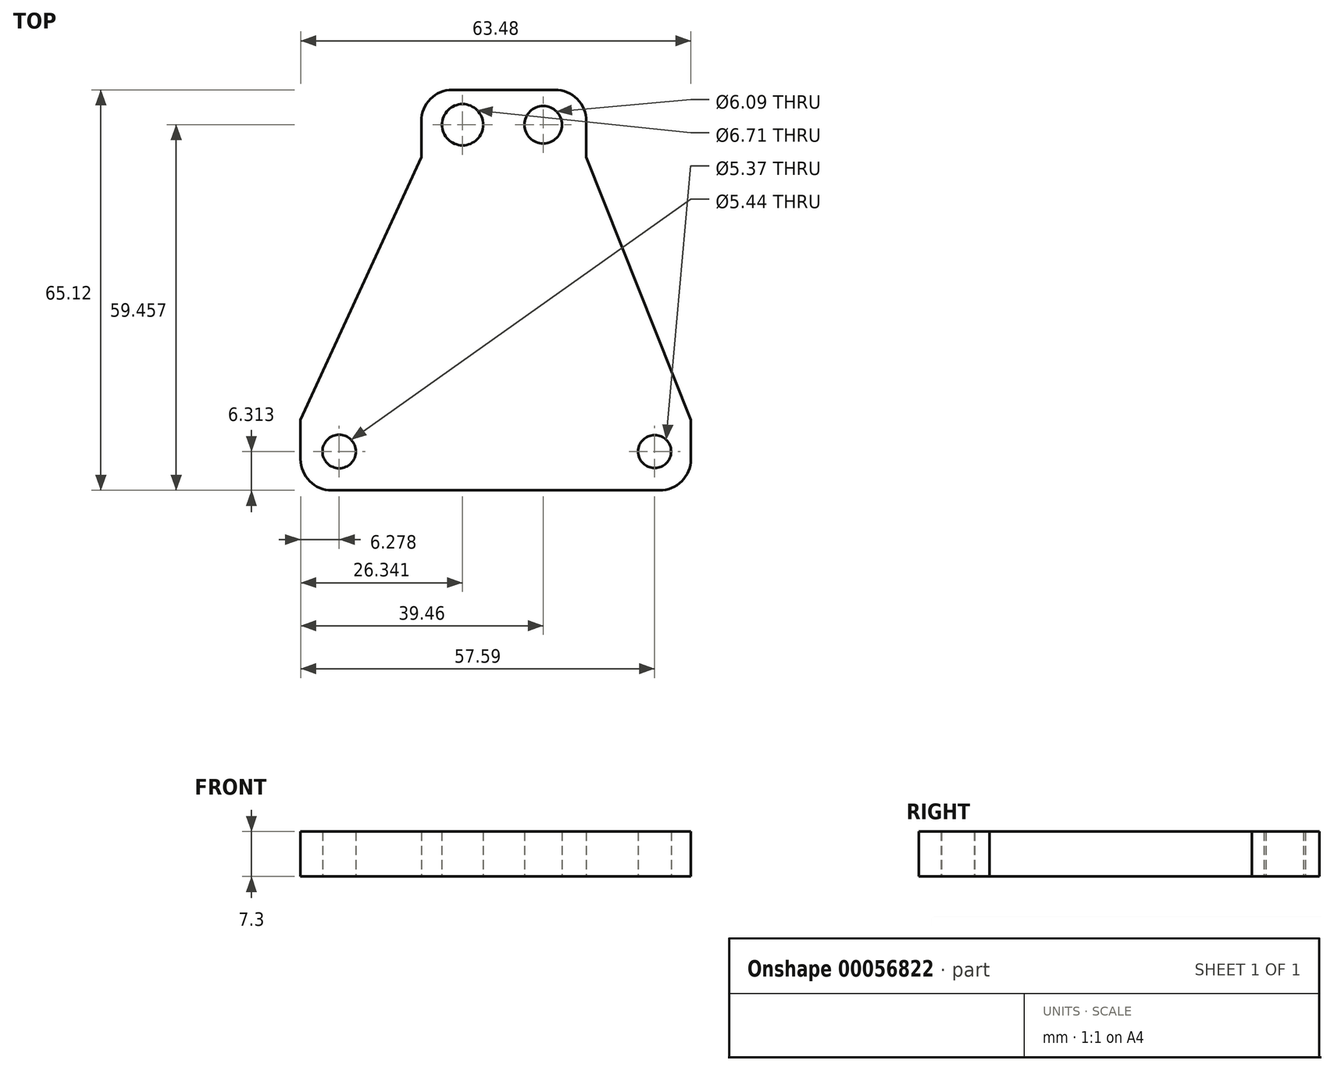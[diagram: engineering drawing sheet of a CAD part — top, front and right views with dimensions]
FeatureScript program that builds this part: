
annotation { "Feature Type Name" : "Feature", "Feature Type Description" : "" }
export const myFeature = defineFeature(function(context is Context, id is Id, definition is map)
    precondition{}
    {
        {
            var Q0;
            Q0=qCreatedBy(makeId("Top.planeOp"),FACE);
            var sketch = newSketch(context, id + "F0", { "sketchPlane" : qUnion([Q0])});
            skLineSegment(sketch, "E0", {"start": v(-57.6, -54.16) * mm, "end": v(5.9, -54.16) * mm});
            skLineSegment(sketch, "E1", {"start": v(-57.6, -54.16) * mm, "end": v(-57.6, -42.7) * mm});
            skLineSegment(sketch, "E2", {"start": v(5.9, -54.16) * mm, "end": v(5.9, -42.7) * mm});
            skLineSegment(sketch, "E3", {"start": v(5.9, -42.7) * mm, "end": v(-11.13, 0) * mm});
            skLineSegment(sketch, "E4", {"start": v(-57.6, -42.7) * mm, "end": v(-37.96, 0) * mm});
            skLineSegment(sketch, "E5", {"start": v(-37.96, 0) * mm, "end": v(-37.96, 10.96) * mm});
            skLineSegment(sketch, "E6", {"start": v(-37.96, 10.96) * mm, "end": v(-11.13, 10.96) * mm});
            skLineSegment(sketch, "E7", {"start": v(-11.13, 10.96) * mm, "end": v(-11.13, 0) * mm});
            skSolve(sketch);
        }
        {
            var Q0;
            Q0 = qSketchRegion(id + "F0", true);
            extrude(context, id + "F1", {"entities" : qUnion([Q0]), "depth" : 7.3 * mm});
        }
        {
            var Q0;
            Q0=qCreatedBy(makeId("Top.planeOp"),FACE);
            var sketch = newSketch(context, id + "F2", { "sketchPlane" : qUnion([Q0])});
            skCircle(sketch, "E8", {"center": v(-31.25, 5.3) * mm, "radius": 3.35 * mm});
            skCircle(sketch, "E9", {"center": v(-18.13, 5.3) * mm, "radius": 3.04 * mm});
            skSolve(sketch);
        }
        {
            var Q0;
            Q0 = qSketchRegion(id + "F2", true);
            extrude(context, id + "F3", {"entities" : qUnion([Q0]), "operationType" : NewBodyOperationType.REMOVE, "depth" : 25.4 * mm});
        }
        {
            var Q0;
            Q0=qCreatedBy(makeId("Top.planeOp"),FACE);
            var sketch = newSketch(context, id + "F4", { "sketchPlane" : qUnion([Q0])});
            skCircle(sketch, "E10", {"center": v(-51.31, -47.85) * mm, "radius": 2.72 * mm});
            skCircle(sketch, "E11", {"center": v(0, -47.85) * mm, "radius": 2.68 * mm});
            skSolve(sketch);
        }
        {
            var Q0;
            Q0 = qSketchRegion(id + "F4", true);
            extrude(context, id + "F5", {"entities" : qUnion([Q0]), "operationType" : NewBodyOperationType.REMOVE, "depth" : 25.4 * mm});
        }
        {
            var Q0;
            Q0=makeQuery(id+"F1.opExtrude","SWEPT_EDGE",EDGE,{"disambiguationData":[OSD([sQuery(id+"F0.wireOp",EDGE,"E0"),sQuery(id+"F0.wireOp",EDGE,"E1")])]});
            var Q1;
            Q1=makeQuery(id+"F1.opExtrude","SWEPT_EDGE",EDGE,{"disambiguationData":[OSD([sQuery(id+"F0.wireOp",EDGE,"E0"),sQuery(id+"F0.wireOp",EDGE,"E2")])]});
            fillet(context, id + "F6", {"entities" : qUnion([Q0, Q1]), "radius" : 5.08 * mm, "tangentPropagation" : true, "allowEdgeOverflow" : false});
        }
        {
            var Q0;
            Q0=makeQuery(id+"F1.opExtrude","SWEPT_EDGE",EDGE,{"disambiguationData":[OSD([sQuery(id+"F0.wireOp",EDGE,"E5"),sQuery(id+"F0.wireOp",EDGE,"E6")])]});
            var Q1;
            Q1=makeQuery(id+"F1.opExtrude","SWEPT_EDGE",EDGE,{"disambiguationData":[OSD([sQuery(id+"F0.wireOp",EDGE,"E6"),sQuery(id+"F0.wireOp",EDGE,"E7")])]});
            fillet(context, id + "F7", {"entities" : qUnion([Q0, Q1]), "radius" : 5.08 * mm, "tangentPropagation" : true, "allowEdgeOverflow" : false});
        }
    });
